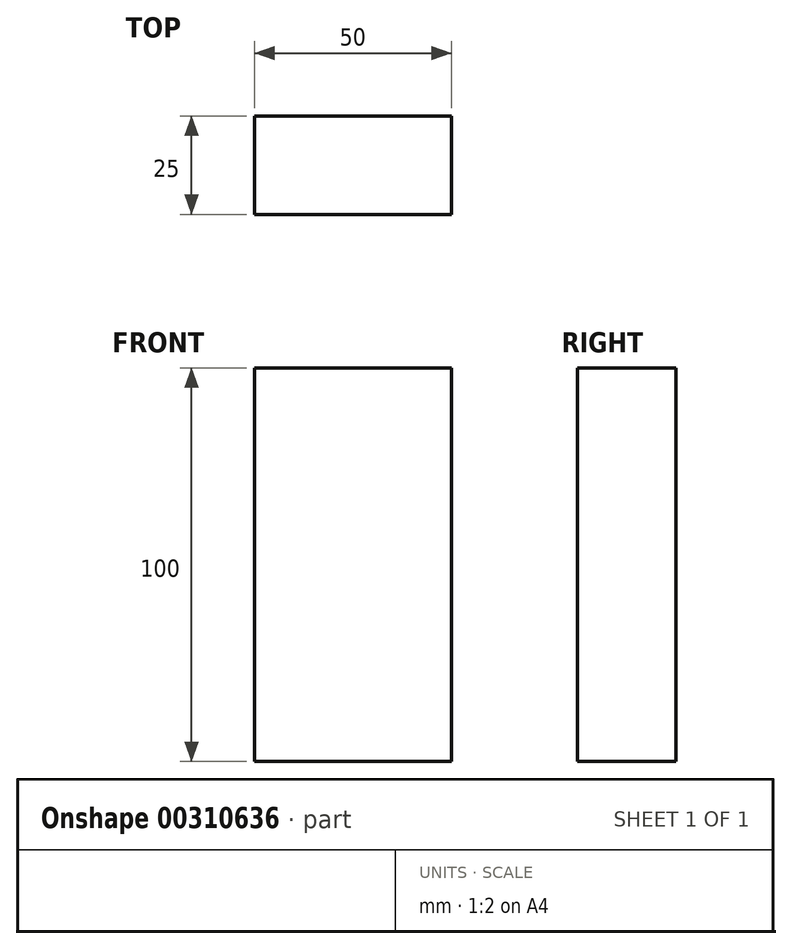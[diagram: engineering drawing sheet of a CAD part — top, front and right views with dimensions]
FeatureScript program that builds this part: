
annotation { "Feature Type Name" : "Feature", "Feature Type Description" : "" }
export const myFeature = defineFeature(function(context is Context, id is Id, definition is map)
    precondition{}
    {
        {
            var Q0;
            Q0=qCreatedBy(makeId("Front.planeOp"),FACE);
            var sketch = newSketch(context, id + "F0", { "sketchPlane" : qUnion([Q0])});
            skLineSegment(sketch, "E0.bottom", {"start": v(0, 0) * mm, "end": v(-50, 0) * mm});
            skLineSegment(sketch, "E0.top", {"start": v(0, 100) * mm, "end": v(-50, 100) * mm});
            skLineSegment(sketch, "E0.left", {"start": v(0, 0) * mm, "end": v(0, 100) * mm});
            skLineSegment(sketch, "E0.right", {"start": v(-50, 0) * mm, "end": v(-50, 100) * mm});
            skSolve(sketch);
        }
        {
            var Q0;
            Q0 = qSketchRegion(id + "F0", true);
            extrude(context, id + "F1", {"entities" : qUnion([Q0]), "depth" : 25 * mm});
        }
    });
